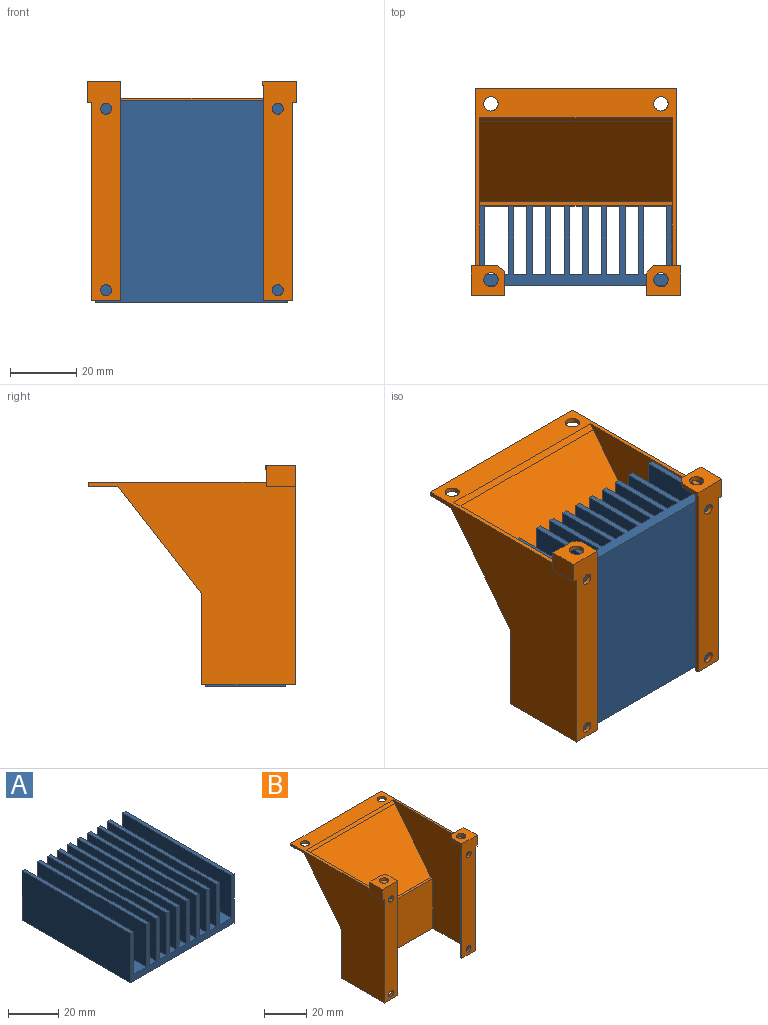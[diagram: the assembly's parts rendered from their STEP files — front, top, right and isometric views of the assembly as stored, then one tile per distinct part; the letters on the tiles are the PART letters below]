
ASSEMBLY  parts=2 mates=1
PART A: 42 faces, bbox 58.2x61.1x24 mm
  f0: plane 61.09x1.65mm, normal (0,0,1), area 100.9mm2, adj f1,f39,f40,f41
  f1: plane 61.09x20.7mm, normal (-1,0,0), area 1264.6mm2, adj f0,f2,f40,f41
  f2: plane 61.09x7.16mm, normal (0,0,1), area 437.6mm2, adj f1,f3,f40,f41
  f3: plane 61.09x20.7mm, normal (1,0,0), area 1264.6mm2, adj f2,f4,f40,f41
  f4: plane 61.09x1.65mm, normal (0,0,1), area 100.9mm2, adj f3,f5,f40,f41
  f5: plane 61.09x24mm, normal (-1,0,0), area 1466.3mm2, adj f4,f6,f40,f41
  f6: plane 61.09x58.17mm, normal (0,0,-1), area 3553.2mm2, adj f5,f7,f40,f41
  f7: plane 61.09x24mm, normal (1,0,0), area 1466.3mm2, adj f6,f8,f40,f41
  f8: plane 61.09x1.65mm, normal (0,0,1), area 100.9mm2, adj f7,f9,f40,f41
  f9: plane 61.09x20.7mm, normal (-1,0,0), area 1264.6mm2, adj f8,f10,f40,f41
  f10: plane 61.09x6.76mm, normal (0,0,1), area 412.7mm2, adj f9,f11,f40,f41
  f11: plane 61.09x20.7mm, normal (1,0,0), area 1264.6mm2, adj f10,f12,f40,f41
  f12: plane 61.09x1.65mm, normal (0,0,1), area 100.9mm2, adj f11,f13,f40,f41
  f13: plane 61.09x20.7mm, normal (-1,0,0), area 1264.6mm2, adj f12,f14,f40,f41
  f14: plane 61.09x3.96mm, normal (0,0,1), area 242.1mm2, adj f13,f15,f40,f41
  f15: plane 61.09x20.7mm, normal (1,0,0), area 1264.6mm2, adj f14,f16,f40,f41
  f16: plane 61.09x1.65mm, normal (0,0,1), area 100.9mm2, adj f15,f17,f40,f41
  f17: plane 61.09x20.7mm, normal (-1,0,0), area 1264.6mm2, adj f16,f18,f40,f41
  f18: plane 61.09x3.96mm, normal (0,0,1), area 242.1mm2, adj f17,f19,f40,f41
  f19: plane 61.09x20.7mm, normal (1,0,0), area 1264.6mm2, adj f18,f20,f40,f41
  f20: plane 61.09x1.65mm, normal (0,0,1), area 100.9mm2, adj f19,f21,f40,f41
  f21: plane 61.09x20.7mm, normal (-1,0,0), area 1264.6mm2, adj f20,f22,f40,f41
  f22: plane 61.09x3.96mm, normal (0,0,1), area 242.1mm2, adj f21,f23,f40,f41
  f23: plane 61.09x20.7mm, normal (1,0,0), area 1264.6mm2, adj f22,f24,f40,f41
  f24: plane 61.09x1.65mm, normal (0,0,1), area 100.9mm2, adj f23,f25,f40,f41
  f25: plane 61.09x20.7mm, normal (-1,0,0), area 1264.6mm2, adj f24,f26,f40,f41
  f26: plane 61.09x3.96mm, normal (0,0,1), area 242.1mm2, adj f25,f27,f40,f41
  f27: plane 61.09x20.7mm, normal (1,0,0), area 1264.6mm2, adj f26,f28,f40,f41
  f28: plane 61.09x1.65mm, normal (0,0,1), area 100.9mm2, adj f27,f29,f40,f41
  f29: plane 61.09x20.7mm, normal (-1,0,0), area 1264.6mm2, adj f28,f30,f40,f41
  f30: plane 61.09x3.96mm, normal (0,0,1), area 242.1mm2, adj f29,f31,f40,f41
  f31: plane 61.09x20.7mm, normal (1,0,0), area 1264.6mm2, adj f30,f32,f40,f41
  f32: plane 61.09x1.65mm, normal (0,0,1), area 100.9mm2, adj f31,f33,f40,f41
  f33: plane 61.09x20.7mm, normal (-1,0,0), area 1264.6mm2, adj f32,f34,f40,f41
  f34: plane 61.09x3.96mm, normal (0,0,1), area 242.1mm2, adj f33,f35,f40,f41
  f35: plane 61.09x20.7mm, normal (1,0,0), area 1264.6mm2, adj f34,f36,f40,f41
  f36: plane 61.09x1.65mm, normal (0,0,1), area 100.9mm2, adj f35,f37,f40,f41
  f37: plane 61.09x20.7mm, normal (-1,0,0), area 1264.6mm2, adj f36,f38,f40,f41
  f38: plane 61.09x3.96mm, normal (0,0,1), area 242.1mm2, adj f37,f39,f40,f41
  f39: plane 61.09x20.7mm, normal (1,0,0), area 1264.6mm2, adj f0,f38,f40,f41
  f40: plane 58.17x24mm, normal (0,-1,0), area 533.8mm2, adj f0,f1,f2,f3,f4,f5,f6,f7
  f41: plane 58.17x24mm, normal (0,1,0), area 533.8mm2, adj f0,f1,f2,f3,f4,f5,f6,f7
PART B: 49 faces, bbox 63.3x62.5x66.2 mm
  f0: plane 8.94x8.94mm, normal (0,0,-1), area 51.7mm2, adj f11,f20,f21,f36,f39,f40,f41,f43
  f1: plane 62.48x61.09mm, normal (1,0,0), area 2170.7mm2, adj f3,f6,f9,f11,f15,f16,f17,f38
  f2: plane 62.48x61.09mm, normal (-1,0,0), area 2170.7mm2, adj f3,f6,f9,f13,f15,f16,f17,f33
  f3: plane 61.21x60.71mm, normal (0,0,1), area 643.3mm2, adj f1,f2,f4,f10,f12,f17,f18,f19
  f4: plane 58.17x1.56mm, normal (0,-0.78,0.62), area 115.6mm2, adj f3,f5,f10,f12
  f5: plane 58.17x30.75mm, normal (0,-0.79,0.62), area 2270.2mm2, adj f4,f10,f12,f14
  f6: plane 60.71x28.32mm, normal (0,0,-1), area 165.2mm2, adj f1,f2,f8,f9,f10,f11,f12,f13
  f7: plane 58.17x1.27mm, normal (0,0,1), area 73.9mm2, adj f8,f10,f12,f14
  f8: plane 58.17x28.75mm, normal (0,-1,0), area 1672.4mm2, adj f6,f7,f10,f12
  f9: plane 60.71x27.48mm, normal (0,1,0), area 1668.4mm2, adj f1,f2,f6,f15
  f10: plane 61.09x52.32mm, normal (-1,0,0), area 2023.8mm2, adj f3,f4,f5,f6,f7,f8,f14,f20
  f11: plane 66.17x10.21mm, normal (0,-1,0), area 579.2mm2, adj f0,f1,f6,f21,f26,f27,f36,f37
  f12: plane 61.09x52.32mm, normal (1,0,0), area 2023.8mm2, adj f3,f4,f5,f6,f7,f8,f14,f22
  f13: plane 66.17x10.17mm, normal (0,-1,0), area 579.2mm2, adj f2,f6,f23,f24,f25,f29,f34,f35
  f14: plane 58.17x0.03mm, normal (0,-1,0), area 1.7mm2, adj f5,f7,f10,f12
  f15: plane 60.71x32.33mm, normal (0,0.79,-0.62), area 2491.3mm2, adj f1,f2,f9,f16
  f16: plane 60.71x8.89mm, normal (0,0,-1), area 510.4mm2, adj f1,f2,f15,f17,f18,f19
  f17: plane 60.71x1.27mm, normal (0,1,0), area 77.1mm2, adj f1,f2,f3,f16
  f18: cylinder r=2.16mm len=4.32mm, axis (0,0,1), area 17.2mm2, adj f3,f16
  f19: cylinder r=2.16mm len=4.32mm, axis (0,0,1), area 17.2mm2, adj f3,f16
  f20: plane 64.9x8.89mm, normal (0,1,0), area 482.2mm2, adj f0,f3,f6,f10,f21,f26,f27,f47
  f21: plane 64.9x1.27mm, normal (-1,0,0), area 82.4mm2, adj f0,f6,f11,f20
  f22: plane 64.9x8.89mm, normal (0,1,0), area 482.5mm2, adj f3,f6,f12,f23,f24,f25,f28,f45
  f23: plane 64.91x1.28mm, normal (1,0,0), area 82.4mm2, adj f6,f13,f22,f29
  f24: cylinder r=1.65mm len=3.3mm, axis (0,-1,0), area 13.2mm2, adj f13,f22
  f25: cylinder r=1.65mm len=3.3mm, axis (0,-1,0), area 13.2mm2, adj f13,f22
  f26: cylinder r=1.65mm len=3.3mm, axis (0,-1,0), area 13.2mm2, adj f11,f20
  f27: cylinder r=1.65mm len=3.3mm, axis (0,-1,0), area 13.2mm2, adj f11,f20
  f28: plane 8.9x7.63mm, normal (0,0,-1), area 51.5mm2, adj f22,f29,f30,f31,f32,f44,f45
  f29: plane 7.29x1.28mm, normal (1,0,0), area 9.2mm2, adj f13,f23,f28,f30,f35
  f30: plane 2.16x1.62mm, normal (0.6,0.8,0), area 3.4mm2, adj f28,f29,f31,f35
  f31: plane 6.74x1.27mm, normal (0,1,0), area 8.6mm2, adj f28,f30,f32,f35
  f32: plane 1.27x0.01mm, normal (-1,0,0), area 0mm2, adj f28,f31,f33,f35
  f33: plane 6.35x1.27mm, normal (0,1,0), area 8.1mm2, adj f2,f32,f34,f35,f45,f46
  f34: plane 8.89x6.35mm, normal (-1,0,0), area 56.5mm2, adj f13,f33,f35,f46
  f35: plane 10.17x8.9mm, normal (0,0,1), area 74.1mm2, adj f13,f29,f30,f31,f32,f33,f34,f44
  f36: plane 6.74x1.27mm, normal (-1,0,0), area 8.6mm2, adj f0,f11,f41,f42
  f37: plane 8.89x6.35mm, normal (1,0,0), area 56.5mm2, adj f11,f38,f42,f48
  f38: plane 6.35x1.27mm, normal (0,1,0), area 8.1mm2, adj f1,f37,f39,f42,f47,f48
  f39: plane 1.27x0.05mm, normal (1,0,0), area 0.1mm2, adj f0,f38,f40,f42
  f40: plane 6.95x1.27mm, normal (0,1,0), area 8.8mm2, adj f0,f39,f41,f42
  f41: plane 2.2x1.99mm, normal (-0.74,0.67,0), area 3.8mm2, adj f0,f36,f40,f42
  f42: plane 10.21x8.94mm, normal (0,0,1), area 74.3mm2, adj f11,f36,f37,f38,f39,f40,f41,f43
  f43: cylinder r=2.16mm len=4.32mm, axis (0,0,1), area 17.2mm2, adj f0,f42
  f44: cylinder r=2.16mm len=4.32mm, axis (0,0,1), area 17.2mm2, adj f28,f35
  f45: plane 7.62x3.81mm, normal (1,0,0), area 29mm2, adj f3,f22,f28,f33
  f46: plane 8.89x1.27mm, normal (0,0,-1), area 11.3mm2, adj f2,f13,f33,f34
  f47: plane 7.62x3.81mm, normal (-1,0,0), area 29mm2, adj f0,f3,f20,f38
  f48: plane 8.89x1.27mm, normal (0,0,-1), area 11.3mm2, adj f1,f11,f37,f38
PLACE A rot(axis=(-1,0,0),90deg) t=(-68.28,-105.83,-34.7)mm
PLACE B t=(-55.11,-66.82,-19.79)mm
MATE planar B.f8 <-> A.f28  axis (0,-1,0) through (-55.11,-68.09,-19.79)mm
